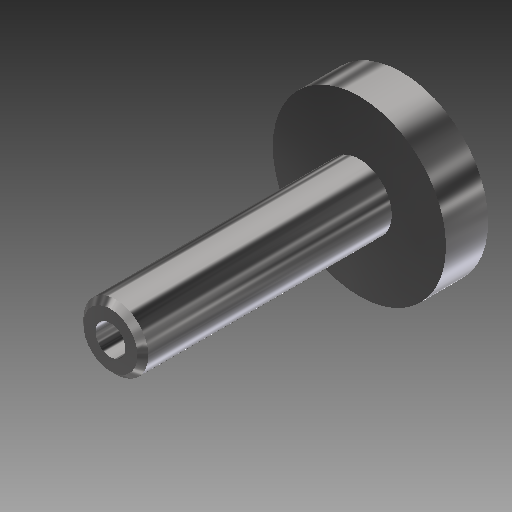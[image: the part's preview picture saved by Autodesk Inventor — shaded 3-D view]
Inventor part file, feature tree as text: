
AUTODESK INVENTOR PART (.ipt)
format: ipt  version: 2017 SP1 (Build 210196100, 196)  size: 158,720 bytes
history: native  units: mm
features: extrude x3, sketch x3, chamfer x1
ambient origin geometry x8: Origin, YZ Plane, XZ Plane, XY Plane, X Axis, Y Axis, Z Axis, Center Point
bodies: Solid1 (feature_tree)
feature tree (7):
  extrude  "Extrusion1"  Depth=7.8mm TaperAngle=0.0deg
  extrude  "Extrusion2"  Depth=46.0mm TaperAngle=0.0deg
  extrude  "Extrusion3"  Depth=15.0mm TaperAngle=0.0deg
  chamfer  "Chamfer1"  Distance=1.0mm Angle=45.0deg
  sketch  "Sketch1"  dims[d0=32.0mm d1=7.8mm d2=0.0mm]
  sketch  "Sketch2"  dims[d3=12.0mm d4=46.0mm d5=0.0mm]
  sketch  "Sketch3"  dims[d6=5.5mm d7=15.0mm d8=0.0mm d9=1.0mm d10=2.0mm d11=45.0deg]
